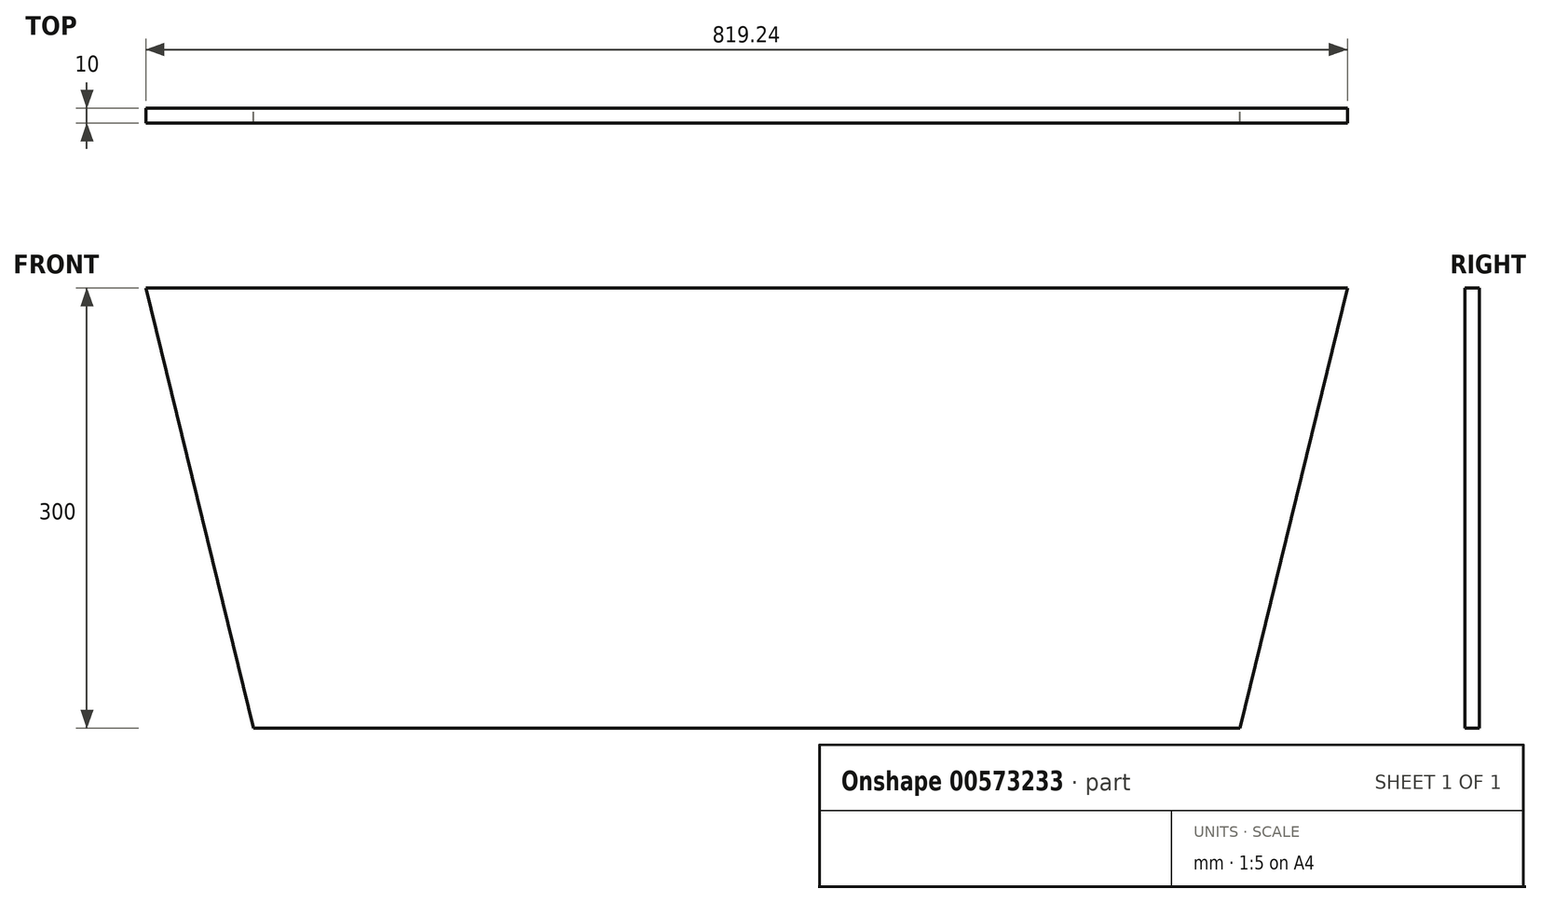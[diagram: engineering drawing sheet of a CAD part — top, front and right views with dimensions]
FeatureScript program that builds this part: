
annotation { "Feature Type Name" : "Feature", "Feature Type Description" : "" }
export const myFeature = defineFeature(function(context is Context, id is Id, definition is map)
    precondition{}
    {
        {
            var Q0;
            Q0=qCreatedBy(makeId("Front.planeOp"),FACE);
            var sketch = newSketch(context, id + "F0", { "sketchPlane" : qUnion([Q0])});
            skLineSegment(sketch, "E0.1", {"start": v(-436.34, 213.95) * mm, "end": v(-436.34, -176.05) * mm});
            skLineSegment(sketch, "E0.3", {"start": v(103.66, 213.95) * mm, "end": v(103.66, -176.05) * mm});
            skLineSegment(sketch, "E1", {"start": v(-465.58, -206.05) * mm, "end": v(133.66, -206.05) * mm});
            skLineSegment(sketch, "E2", {"start": v(-436.34, -176.05) * mm, "end": v(103.66, -176.05) * mm});
            skLineSegment(sketch, "E3", {"start": v(-436.34, 213.95) * mm, "end": v(103.66, 213.95) * mm});
            skLineSegment(sketch, "E4", {"start": v(-465.58, 243.95) * mm, "end": v(133.66, 243.95) * mm});
            skLineSegment(sketch, "E5", {"start": v(-465.58, 243.95) * mm, "end": v(-575.58, 243.95) * mm});
            skLineSegment(sketch, "E6", {"start": v(133.66, 243.95) * mm, "end": v(243.66, 243.95) * mm});
            skLineSegment(sketch, "E7", {"start": v(-575.58, 243.95) * mm, "end": v(-465.58, -206.05) * mm});
            skLineSegment(sketch, "E8", {"start": v(243.66, 243.95) * mm, "end": v(133.66, -206.05) * mm});
            skLineSegment(sketch, "E9.0", {"start": v(-537.36, 213.95) * mm, "end": v(-495.58, 43.02) * mm});
            skLineSegment(sketch, "E9.1", {"start": v(-495.58, 213.95) * mm, "end": v(-537.36, 213.95) * mm});
            skLineSegment(sketch, "E9.2", {"start": v(-495.58, 213.95) * mm, "end": v(-495.58, 43.02) * mm});
            skLineSegment(sketch, "E10.0", {"start": v(205.44, 213.95) * mm, "end": v(163.66, 43.02) * mm});
            skLineSegment(sketch, "E10.1", {"start": v(163.66, 213.95) * mm, "end": v(205.44, 213.95) * mm});
            skLineSegment(sketch, "E10.2", {"start": v(163.66, 213.95) * mm, "end": v(163.66, 43.02) * mm});
            skSolve(sketch);
        }
        {
            var Q0;
            Q0=makeQuery(id+"F0.imprint","IMPRINT",FACE,{"disambiguationData":[TD([[makeQuery(id+"F0.imprint","IMPRINT",EDGE,{"derivedFrom":sQuery(id+"F0.wireOp",EDGE,"E0.1")}),-1.0]])]});
            extrude(context, id + "F1", {"entities" : qUnion([Q0]), "depth" : 10 * mm, "offsetDistance" : 25 * mm});
        }
        {
            var Q0;
            Q0=makeQuery(id+"F1.opExtrude","CAP_FACE",FACE,{"disambiguationData":[OSD([sQuery(id+"F0.wireOp",EDGE,"E0.1"),sQuery(id+"F0.wireOp",EDGE,"E0.3"),sQuery(id+"F0.wireOp",EDGE,"E1"),sQuery(id+"F0.wireOp",EDGE,"E2"),sQuery(id+"F0.wireOp",EDGE,"E3"),sQuery(id+"F0.wireOp",EDGE,"E4"),sQuery(id+"F0.wireOp",EDGE,"E5"),sQuery(id+"F0.wireOp",EDGE,"E6"),sQuery(id+"F0.wireOp",EDGE,"E7"),sQuery(id+"F0.wireOp",EDGE,"E8"),sQuery(id+"F0.wireOp",EDGE,"E9.0"),sQuery(id+"F0.wireOp",EDGE,"E9.1"),sQuery(id+"F0.wireOp",EDGE,"E9.2"),sQuery(id+"F0.wireOp",EDGE,"E10.0"),sQuery(id+"F0.wireOp",EDGE,"E10.1"),sQuery(id+"F0.wireOp",EDGE,"E10.2")])],"isStart":false});
            var sketch = newSketch(context, id + "F2", { "sketchPlane" : qUnion([Q0])});
            skLineSegment(sketch, "E11", {"start": v(-575.58, 243.95) * mm, "end": v(243.66, 243.95) * mm});
            skLineSegment(sketch, "E12", {"start": v(-575.58, 243.95) * mm, "end": v(-502.25, -56.05) * mm});
            skLineSegment(sketch, "E13", {"start": v(-237.4, -56.05) * mm, "end": v(-502.25, -56.05) * mm});
            skLineSegment(sketch, "E14", {"start": v(-237.4, -56.05) * mm, "end": v(170.33, -56.05) * mm});
            skLineSegment(sketch, "E15", {"start": v(170.33, -56.05) * mm, "end": v(243.66, 243.95) * mm});
            skLineSegment(sketch, "E16", {"start": v(-237.4, 243.95) * mm, "end": v(243.66, 243.95) * mm});
            skLineSegment(sketch, "E17", {"start": v(-237.4, 243.95) * mm, "end": v(-575.58, 243.95) * mm});
            skSolve(sketch);
        }
        {
            var Q0;
            {var subQ0=makeQuery(id+"F1.opExtrude","CAP_EDGE",EDGE,{"disambiguationData":[OSD([sQuery(id+"F0.wireOp",EDGE,"E3")])],"isStart":false});Q0=makeQuery(id+"F2.imprint","IMPRINT",FACE,{"disambiguationData":[TD([[makeQuery(id+"F2.imprint","IMPRINT",EDGE,{"derivedFrom":subQ0}),-1.0]])]});}
            var Q1;
            {var subQ1=sQuery(id+"F2.wireOp",EDGE,"E12");Q1=makeQuery(id+"F2.imprint","IMPRINT",FACE,{"disambiguationData":[TD([[makeQuery(id+"F2.imprint","IMPRINT",EDGE,{"derivedFrom":subQ1}),1.0]])]});}
            var Q2;
            Q2=makeQuery(id+"F2.imprint","IMPRINT",FACE,{"disambiguationData":[TD([[makeQuery(id+"F2.imprint","IMPRINT",EDGE,{"derivedFrom":makeQuery(id+"F1.opExtrude","CAP_EDGE",EDGE,{"disambiguationData":[OSD([sQuery(id+"F0.wireOp",EDGE,"E9.0")])],"isStart":false})}),1.0]])]});
            var Q3;
            Q3=makeQuery(id+"F2.imprint","IMPRINT",FACE,{"disambiguationData":[TD([[makeQuery(id+"F2.imprint","IMPRINT",EDGE,{"derivedFrom":makeQuery(id+"F1.opExtrude","CAP_EDGE",EDGE,{"disambiguationData":[OSD([sQuery(id+"F0.wireOp",EDGE,"E10.0")])],"isStart":false})}),-1.0]])]});
            extrude(context, id + "F3", {"entities" : qUnion([Q0, Q1, Q2, Q3]), "operationType" : NewBodyOperationType.ADD, "depth" : 10 * mm, "offsetDistance" : 25 * mm});
        }
        {
            var Q0;
            Q0=makeQuery(id+"F1.opExtrude","CAP_FACE",FACE,{"disambiguationData":[OSD([sQuery(id+"F0.wireOp",EDGE,"E0.1"),sQuery(id+"F0.wireOp",EDGE,"E0.3"),sQuery(id+"F0.wireOp",EDGE,"E1"),sQuery(id+"F0.wireOp",EDGE,"E2"),sQuery(id+"F0.wireOp",EDGE,"E3"),sQuery(id+"F0.wireOp",EDGE,"E4"),sQuery(id+"F0.wireOp",EDGE,"E5"),sQuery(id+"F0.wireOp",EDGE,"E6"),sQuery(id+"F0.wireOp",EDGE,"E7"),sQuery(id+"F0.wireOp",EDGE,"E8"),sQuery(id+"F0.wireOp",EDGE,"E9.0"),sQuery(id+"F0.wireOp",EDGE,"E9.1"),sQuery(id+"F0.wireOp",EDGE,"E9.2"),sQuery(id+"F0.wireOp",EDGE,"E10.0"),sQuery(id+"F0.wireOp",EDGE,"E10.1"),sQuery(id+"F0.wireOp",EDGE,"E10.2")])],"isStart":false});
            extrude(context, id + "F4", {"entities" : qUnion([Q0]), "operationType" : NewBodyOperationType.REMOVE, "endBound" : BoundingType.THROUGH_ALL, "oppositeDirection" : true, "depth" : 25 * mm, "offsetDistance" : 25 * mm});
        }
        {
            var Q0;
            Q0=makeQuery(id+"F0.imprint","IMPRINT",FACE,{"disambiguationData":[TD([[makeQuery(id+"F0.imprint","IMPRINT",EDGE,{"derivedFrom":sQuery(id+"F0.wireOp",EDGE,"E0.1")}),-1.0]])]});
            extrude(context, id + "F5", {"entities" : qUnion([Q0]), "operationType" : NewBodyOperationType.REMOVE, "depth" : 10 * mm, "offsetDistance" : 25 * mm});
        }
    });
